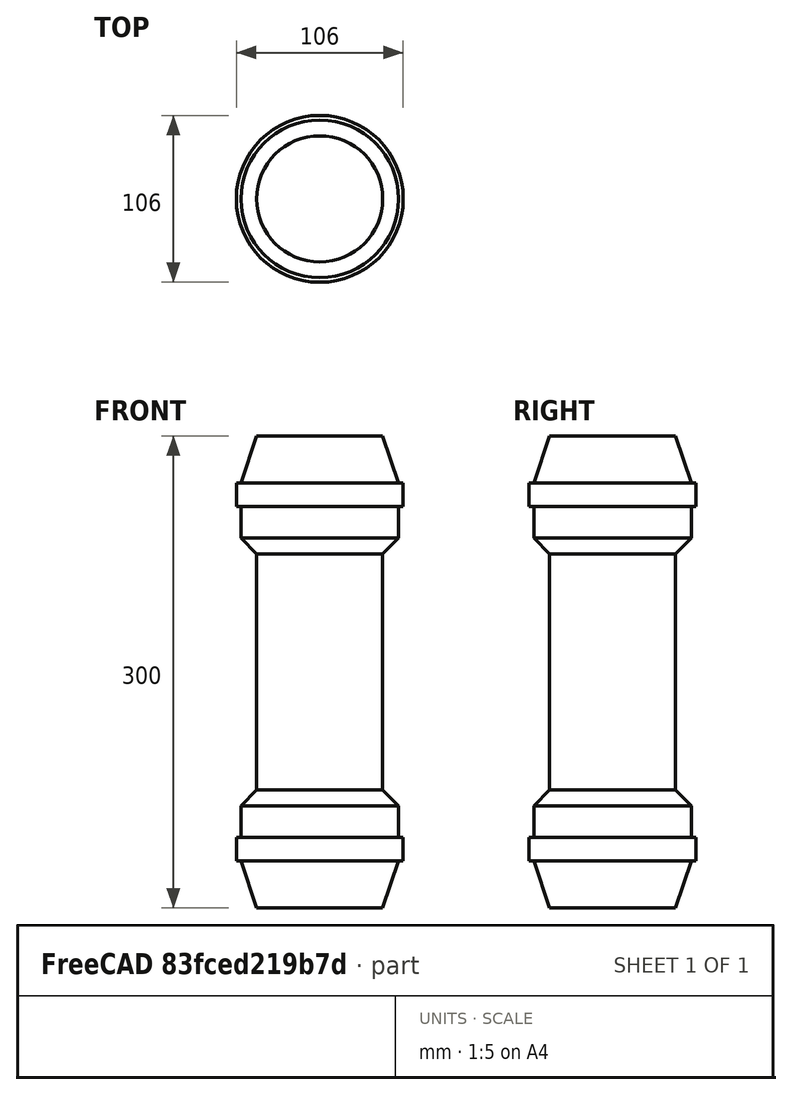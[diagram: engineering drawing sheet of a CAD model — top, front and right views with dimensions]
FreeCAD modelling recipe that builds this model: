
FCSTD DOCUMENT  (FreeCAD 1.0R39285 (Git))
Label: carria
License: All rights reserved
LicenseURL: https://en.wikipedia.org/wiki/All_rights_reserved
objects: Sketcher::SketchObject×1, PartDesign::Revolution×1, PartDesign::Body×1
note: 6 computed .brp shape members not serialized (recipe doc carries the construction recipe); baked Part::Feature solids carry a one-line shape summary decoded from their .brp

FEATURE [Sketcher::SketchObject] Sketch
  ArcFitTolerance = 1e-06
  AttachmentSupport = -> [XZ_Plane]
  FullyConstrained = true
  MakeInternals = false
  MapMode = 5
  Placement = pos=(0,0,0) rot=(1,0,0;1.5708rad)
  sketch-geometry (16):
    g0: LineSegment StartX=0 StartY=150 StartZ=0 EndX=40 EndY=150 EndZ=0
    g1: LineSegment StartX=40 StartY=150 StartZ=0 EndX=50 EndY=120 EndZ=0
    g2: LineSegment StartX=50 StartY=120 StartZ=0 EndX=53 EndY=120 EndZ=0
    g3: LineSegment StartX=53 StartY=120 StartZ=0 EndX=53 EndY=105 EndZ=0
    g4: LineSegment StartX=53 StartY=105 StartZ=0 EndX=50 EndY=105 EndZ=0
    g5: LineSegment StartX=50 StartY=-105 StartZ=0 EndX=53 EndY=-105 EndZ=0
    g6: LineSegment StartX=53 StartY=-105 StartZ=0 EndX=53 EndY=-120 EndZ=0
    g7: LineSegment StartX=53 StartY=-120 StartZ=0 EndX=50 EndY=-120 EndZ=0
    g8: LineSegment StartX=50 StartY=-120 StartZ=0 EndX=40 EndY=-150 EndZ=0
    g9: LineSegment StartX=40 StartY=-150 StartZ=0 EndX=0 EndY=-150 EndZ=0
    g10: LineSegment StartX=0 StartY=-150 StartZ=0 EndX=0 EndY=150 EndZ=0
    g11: LineSegment StartX=50 StartY=105 StartZ=0 EndX=50 EndY=85 EndZ=0
    g12: LineSegment StartX=50 StartY=85 StartZ=0 EndX=40 EndY=75 EndZ=0
    g13: LineSegment StartX=40 StartY=75 StartZ=0 EndX=40 EndY=-75 EndZ=0
    g14: LineSegment StartX=40 StartY=-75 StartZ=0 EndX=50 EndY=-85 EndZ=0
    g15: LineSegment StartX=50 StartY=-85 StartZ=0 EndX=50 EndY=-105 EndZ=0
  constraints (48):
    c: PointOnObject(g0,g-2)
    c: Horizontal(g0)
    c: Coincident(g0,g1)
    c: Coincident(g1,g2)
    c: Horizontal(g2)
    c: Coincident(g2,g3)
    c: Coincident(g3,g4)
    c: Horizontal(g4)
    c: Horizontal(g5)
    c: Coincident(g5,g6)
    c: Coincident(g6,g7)
    c: Coincident(g7,g8)
    c: Coincident(g8,g9)
    c: PointOnObject(g9,g-2)
    c: Coincident(g9,g10)
    c: Coincident(g10,g0)
    c: Vertical(g3)
    c: Horizontal(g7)
    c: Vertical(g6)
    c: Vertical(g5,g7)
    c: Horizontal(g9)
    c: Vertical(g4,g1)
    c: Vertical(g0,g8)
    c: Vertical(g5,g3)
    c: DistanceX(g2,g2) = 3
    c: DistanceY(g3,g3) = 15
    c: Equal(g3,g6)
    c: DistanceY(g10,g10) = 300
    c: DistanceX(g-1,g1) = 50
    c: DistanceY(g5,g4) = 210
    c: Equal(g8,g1)
    c: DistanceY(g9,g-1) = 150
    c: Distance(g0,g0) = 40
    c: Coincident(g4,g11)
    c: Vertical(g11)
    c: Coincident(g11,g12)
    c: Coincident(g12,g13)
    c: Vertical(g13)
    c: Coincident(g13,g14)
    c: Coincident(g14,g15)
    c: Coincident(g15,g5)
    c: Vertical(g15)
    c: Vertical(g14,g11)
    c: Equal(g12,g14)
    c: DistanceY(g13,g13) = 150
    c: DistanceY(g12,g4) = 30
    c: DistanceX(g12,g12) = 10
    c: DistanceY(g15,g15) = 20
FEATURE [PartDesign::Revolution] Revolution
  Angle = 360
  Angle2 = 60
  Axis = (0,2e-16,1)
  Base = (0,0,0)
  Placement = pos=(0,0,0) rot=(1,0,0;1.5708rad)
  Profile = -> Sketch
  ReferenceAxis = -> Sketch [V_Axis]
  Refine = true
  Reversed = true
  Suppressed = false
  Type = 0
FEATURE [PartDesign::Body] Body
  AllowCompound = false
  Group = -> [Sketch,Revolution]
  Origin = -> Origin
  Tip = -> Revolution
